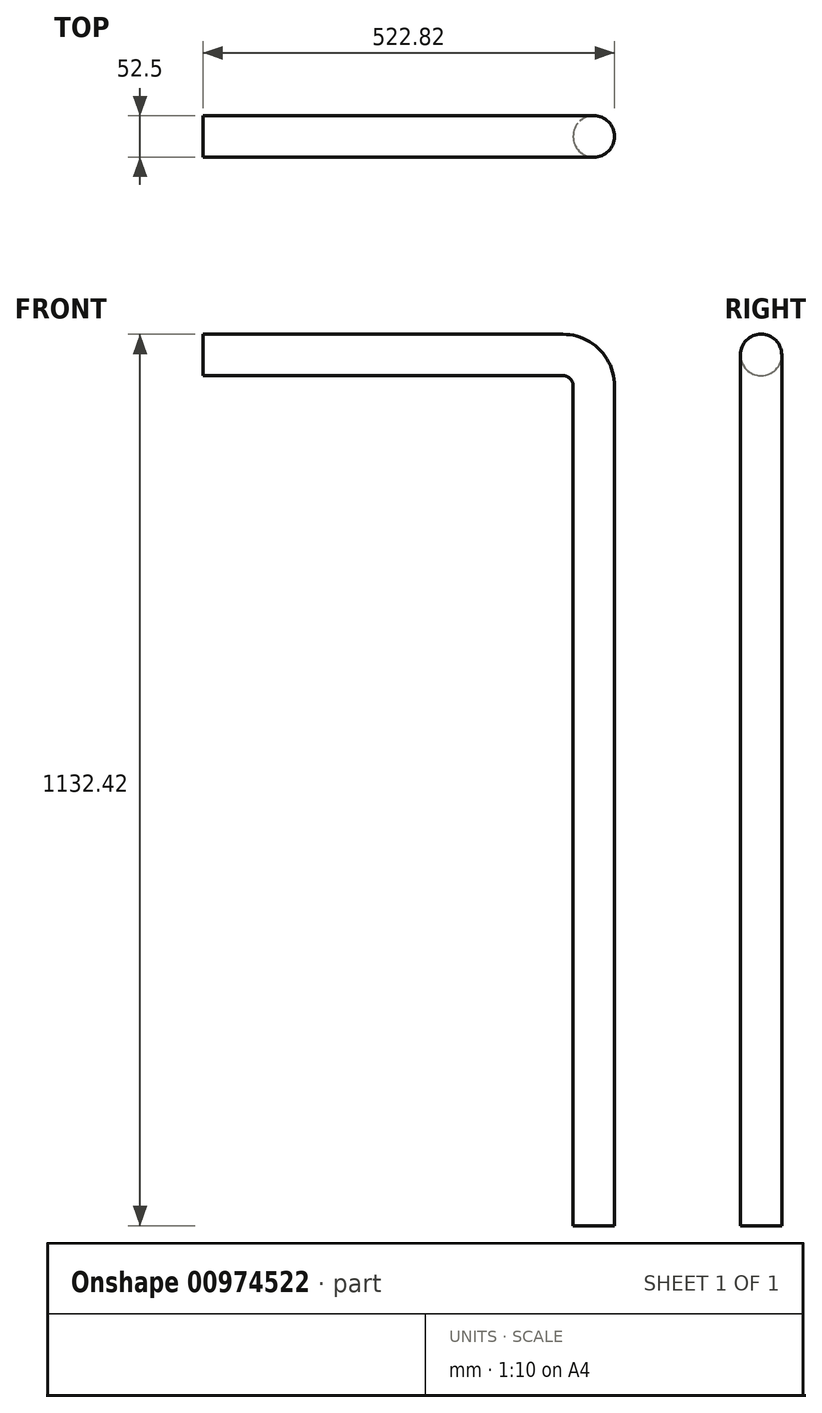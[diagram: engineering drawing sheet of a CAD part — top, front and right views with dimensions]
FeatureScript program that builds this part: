
annotation { "Feature Type Name" : "Feature", "Feature Type Description" : "" }
export const myFeature = defineFeature(function(context is Context, id is Id, definition is map)
    precondition{}
    {
        {
            var Q0;
            Q0=qCreatedBy(makeId("Right.planeOp"),FACE);
            var sketch = newSketch(context, id + "F0", { "sketchPlane" : qUnion([Q0])});
            skCircle(sketch, "E0", {"center": v(0, 0) * mm, "radius": 26.25 * mm});
            skSolve(sketch);
        }
        {
            var Q0;
            Q0=qCreatedBy(makeId("Front.planeOp"),FACE);
            var sketch = newSketch(context, id + "F1", { "sketchPlane" : qUnion([Q0])});
            skArc(sketch, "E1", {"start": v(0, 0) * mm, "mid": v(27.84, -11.53) * mm, "end": v(39.37, -39.37) * mm});
            skLineSegment(sketch, "E2.0", {"start": v(0, 26.25) * mm, "end": v(0, -26.25) * mm, "construction": true});
            skSolve(sketch);
        }
        {
            var Q0;
            Q0=makeQuery(id+"F0.imprint","IMPRINT",FACE,{"disambiguationData":[TD([[makeQuery(id+"F0.imprint","IMPRINT",EDGE,{"derivedFrom":sQuery(id+"F0.wireOp",EDGE,"E0")}),1.0]])]});
            var Q1;
            Q1=qConstructionFilter(qBodyType(qCreatedBy(id+"F1",EDGE),BodyType.WIRE),ConstructionObject.NO);
            sweep(context, id + "F2", {"profiles" : qUnion([Q0]), "path" : qUnion([Q1])});
        }
        {
            var Q0;
            Q0=makeQuery(id+"F2.opSweep","CAP_FACE",FACE,{"disambiguationData":[OSD([sQuery(id+"F0.wireOp",EDGE,"E0"),sQuery(id+"F1.wireOp",VERTEX,"E1.start")])],"isStart":true});
            extrude(context, id + "F3", {"entities" : qUnion([Q0]), "operationType" : NewBodyOperationType.ADD, "depth" : 457.2 * mm, "offsetDistance" : 25.4 * mm});
        }
        {
            var Q0;
            Q0=makeQuery(id+"F2.opSweep","CAP_FACE",FACE,{"disambiguationData":[OSD([sQuery(id+"F0.wireOp",EDGE,"E0"),sQuery(id+"F1.wireOp",VERTEX,"E1.end")])],"isStart":false});
            extrude(context, id + "F4", {"entities" : qUnion([Q0]), "operationType" : NewBodyOperationType.ADD, "depth" : 1066.8 * mm, "offsetDistance" : 25.4 * mm});
        }
    });
